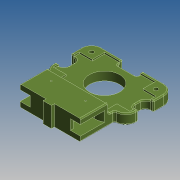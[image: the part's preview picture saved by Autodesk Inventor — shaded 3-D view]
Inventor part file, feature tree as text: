
AUTODESK INVENTOR PART (.ipt)
format: ipt  version: 2015 SP1 (Build 190203100, 203)  size: 659,968 bytes
history: native  units: mm
features: fillet x15, sketch x14, extrude x9, projected_geometry x6, hole x5, mirror x4, other x1
ambient origin geometry x8: Origin, YZ Plane, XZ Plane, XY Plane, X Axis, Y Axis, Z Axis, Center Point
bodies: Solid2 (feature_tree)
feature tree (54):
  extrude  "Extrusion2"  Depth=3.0mm
  extrude  "Extrusion3"  Depth=10.0mm TaperAngle=0.0deg
  hole  "Trou pour ressort"  [1 undecoded]
  mirror  "Mirror1"
  extrude  "Extrusion5"  Depth=3.0mm
  extrude  "Extrusion6"  Depth=2.0mm TaperAngle=0.0deg
  fillet  "Fillet3"  Radius=3.0mm
  hole  "Hole5"  [1 undecoded]
  extrude  "Extrusion13"  Depth=10.0mm TaperAngle=0.0deg
  other  "Work Axis2"
  hole  "Hole12"  [1 undecoded]
  mirror  "Mirror4"
  hole  "Hole16"  [1 undecoded]
  extrude  "Extrusion20"  Depth=41.0mm
  fillet  "Fillet30"  Radius=41.0mm
  fillet  "Fillet31"  Radius=20.0mm
  extrude  "Extrusion21"  Depth=10.0mm TaperAngle=0.0deg
  extrude  "Extrusion22"  Depth=10.0mm
  fillet  "Fillet32"  Radius=10.0mm
  fillet  "Fillet33"  Radius=76.2mm
  mirror  "Mirror6"
  fillet  "Fillet34"  Radius=26.0mm
  fillet  "Fillet35"  Radius=1.5mm
  extrude  "Extrusion23"  Depth=50.5mm
  fillet  "Fillet36"  Radius=50.5mm
  fillet  "Fillet37"  Radius=8.0mm
  fillet  "Fillet38"  Radius=15.0mm
  fillet  "Fillet39"  Radius=2.0mm
  fillet  "Fillet42"  Radius=1.0mm
  hole  "Hole17"  [1 undecoded]
  mirror  "Mirror7"
  fillet  "Fillet43"  Radius=5.0mm
  fillet  "Fillet45"  Radius=1.0mm
  fillet  "Fillet46"  Radius=20.0mm
  sketch  "Sketch1"  dims[d14=20.0mm d15=20.0mm d16=0.0mm d19=3.0mm]
  sketch  "Sketch3"  dims[d20=5.0mm d21=10.0mm d22=0.0mm]
  sketch  "Sketch6"  dims[d42=22.0mm d43=4.1mm]
  sketch  "Sketch8"  dims[d44=30.0mm d45=3.0mm]
  sketch  "Sketch9"  dims[d49=4.0mm]
  sketch  "Sketch12"  dims[d50=5.0mm d51=6.0mm d52=4.0mm d53=2.0mm d54=90.0deg d55=8.0mm d56=20.594885mm d60=2.0mm d61=0.0mm d62=3.0mm]
  sketch  "Sketch22"  dims[d66=16.0mm d67=58.0mm d68=0.0mm]
  sketch  "Sketch29"  dims[d78=11.5mm]
  projected_geometry  "Projected Loop2"
  sketch  "Sketch36"  dims[d79=6.0mm d80=6.0mm d81=4.0mm d82=2.0mm d83=90.0deg d84=8.0mm d85=20.594885mm d147=10.0mm d148=0.0mm]
  sketch  "Sketch38"  dims[d205=3.0mm]
  sketch  "Sketch39"  dims[d206=1.5mm d207=6.0mm d208=4.0mm d209=2.0mm d210=90.0deg d211=2.0mm d212=20.594885mm d213=10.0mm]
  sketch  "Sketch40"  dims[d245=20.0mm d246=17.0mm]
  sketch  "Sketch41"  dims[d258=32.0mm]
  sketch  "Sketch43"  dims[d259=30.0mm d260=6.0mm d261=4.0mm d262=2.0mm d263=90.0deg d264=8.0mm d265=20.594885mm d266=41.0mm d267=41.0mm d272=20.0mm d273=10.0mm d274=0.0mm d275=10.0mm d276=10.0mm d277=76.2mm d278=26.0mm d279=1.5mm d280=0.0mm d281=50.5mm d282=50.5mm d283=8.0mm d284=15.0mm d285=2.0mm d286=0.0mm d287=1.0mm d288=5.0mm d289=5.0mm d290=1.0mm d291=20.0mm d292=6.0mm d293=2.0mm d294=0.0mm d295=1.0mm d296=2.0mm d297=2.0mm d298=1.0mm d303=1.0mm d304=32.0mm d305=51.0mm d306=4.0mm d307=6.0mm d308=4.0mm d309=2.0mm d310=90.0deg d311=8.0mm d312=20.594885mm d313=2.0mm d315=2.0mm d316=1.0mm]
  projected_geometry  "Project Cut Edges2"
  projected_geometry  "Project Cut Edges4"
  projected_geometry  "Project Cut Edges5"
  projected_geometry  "Project Cut Edges7"
  projected_geometry  "Project Cut Edges9"
note: 5 required parameter values undecoded (feature->parameter linkage not recoverable at this tier; creation-order binding heuristic only, values carry confidence <= 0.55)
